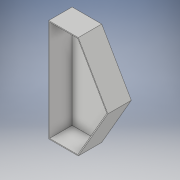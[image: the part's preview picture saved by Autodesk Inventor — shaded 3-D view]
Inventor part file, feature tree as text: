
AUTODESK INVENTOR PART (.ipt)
format: ipt  version: 2019 (Build 230136000, 136)  size: 100,864 bytes
history: native  units: mm
features: extrude x1, shell x1, sketch x1
ambient origin geometry x8: Origin, YZ Plane, XZ Plane, XY Plane, X Axis, Y Axis, Z Axis, Center Point
bodies: Solid1 (feature_tree)
feature tree (3):
  extrude  "Extrusion1"  Depth=1.5mm
  shell  "Shell1"  [1 undecoded]
  sketch  "Sketch1"  dims[d1=40.0mm d2=0.0mm d3=1.5mm]
note: 1 required parameter value undecoded (feature->parameter linkage not recoverable at this tier; creation-order binding heuristic only, values carry confidence <= 0.55)
